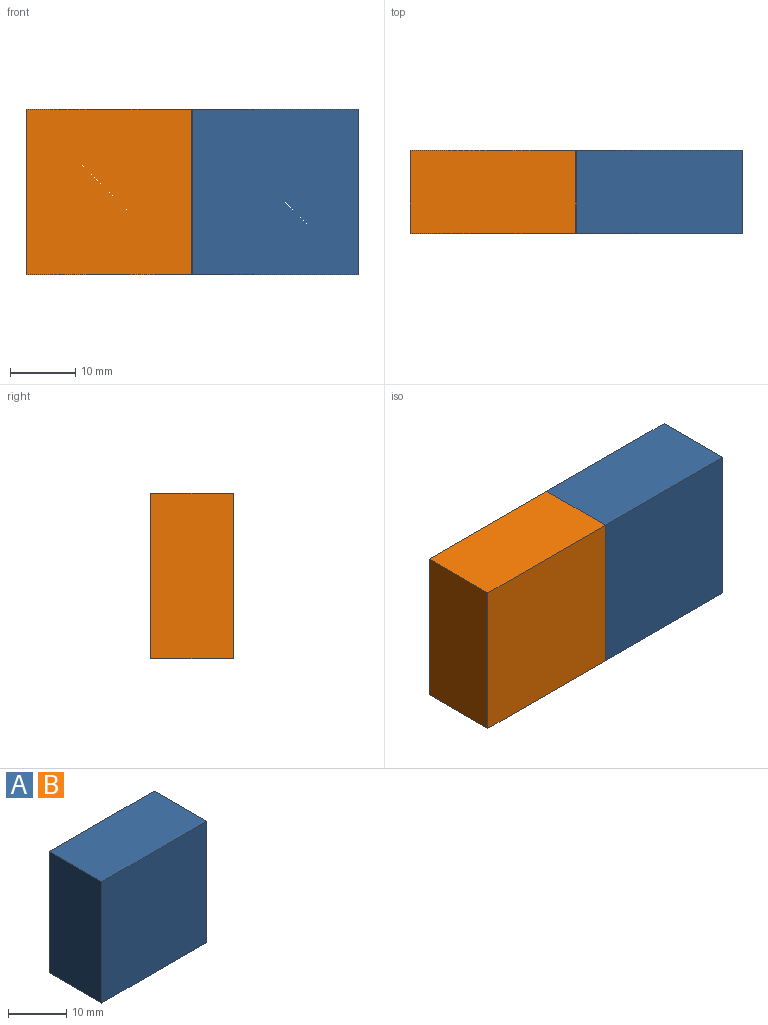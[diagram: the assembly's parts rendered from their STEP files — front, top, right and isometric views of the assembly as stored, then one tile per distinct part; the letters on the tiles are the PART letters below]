
ASSEMBLY  parts=2 mates=1
PART A: 6 faces, bbox 25.4x12.7x25.4 mm
  f0: plane 25.4x12.7mm, normal (0,0,1), area 322.6mm2, adj f1,f3,f4,f5
  f1: plane 25.4x12.7mm, normal (-1,0,0), area 322.6mm2, adj f0,f2,f4,f5
  f2: plane 25.4x12.7mm, normal (0,0,-1), area 322.6mm2, adj f1,f3,f4,f5
  f3: plane 25.4x12.7mm, normal (1,0,0), area 322.6mm2, adj f0,f2,f4,f5
  f4: plane 25.4x25.4mm, normal (0,-1,0), area 645.2mm2, adj f0,f1,f2,f3
  f5: plane 25.4x25.4mm, normal (0,1,0), area 645.2mm2, adj f0,f1,f2,f3
PART B: same geometry as A
PLACE A t=(8.52,-5.7,4.21)mm
PLACE B t=(-16.88,-5.7,4.21)mm
MATE fastened A.f4 <-> B.f4  axis (0,-1,0) through (-58.26,-18.4,43.38)mm
